# Revit family: Clapeta antiretur PP
name_source: partatom
category: Pipe Fittings
units: mm (PartAtom-declared; Revit-internal decimal feet)

## family parameters
Always vertical = No
Cut with Voids When Loaded = No
OmniClass Number = 23.60.30.11.14
OmniClass Title = Pipework Fittings
Part Type = Transition
Round Connector Dimension = Use Diameter
Shared = No
Work Plane-Based = No

## types (1)
- Clapeta antiretur PP
    A = 68 mm  [stored 0.223097 ft]
    B = 92 mm  [stored 0.301837 ft]
    Cod Articol Teraplast = FVE0365
    D = 50 mm  [stored 0.164042 ft]
    Description = Sistem de tevi si fitinguri din PP pentru canalizari interioare.
    L = 169 mm  [stored 0.554462 ft]
    Manufacturer = Teraplast
    O1 = 2 mm  [stored 0.00656168 ft]
    URL = https://www.teraplast.ro

note: [stored X ft] marks values corroborated as IEEE doubles in the binary element streams (Revit-internal decimal feet)

## geometry (parser evidence)
native form markers: Sweep x3
no freeform markers — native parametric forms only
